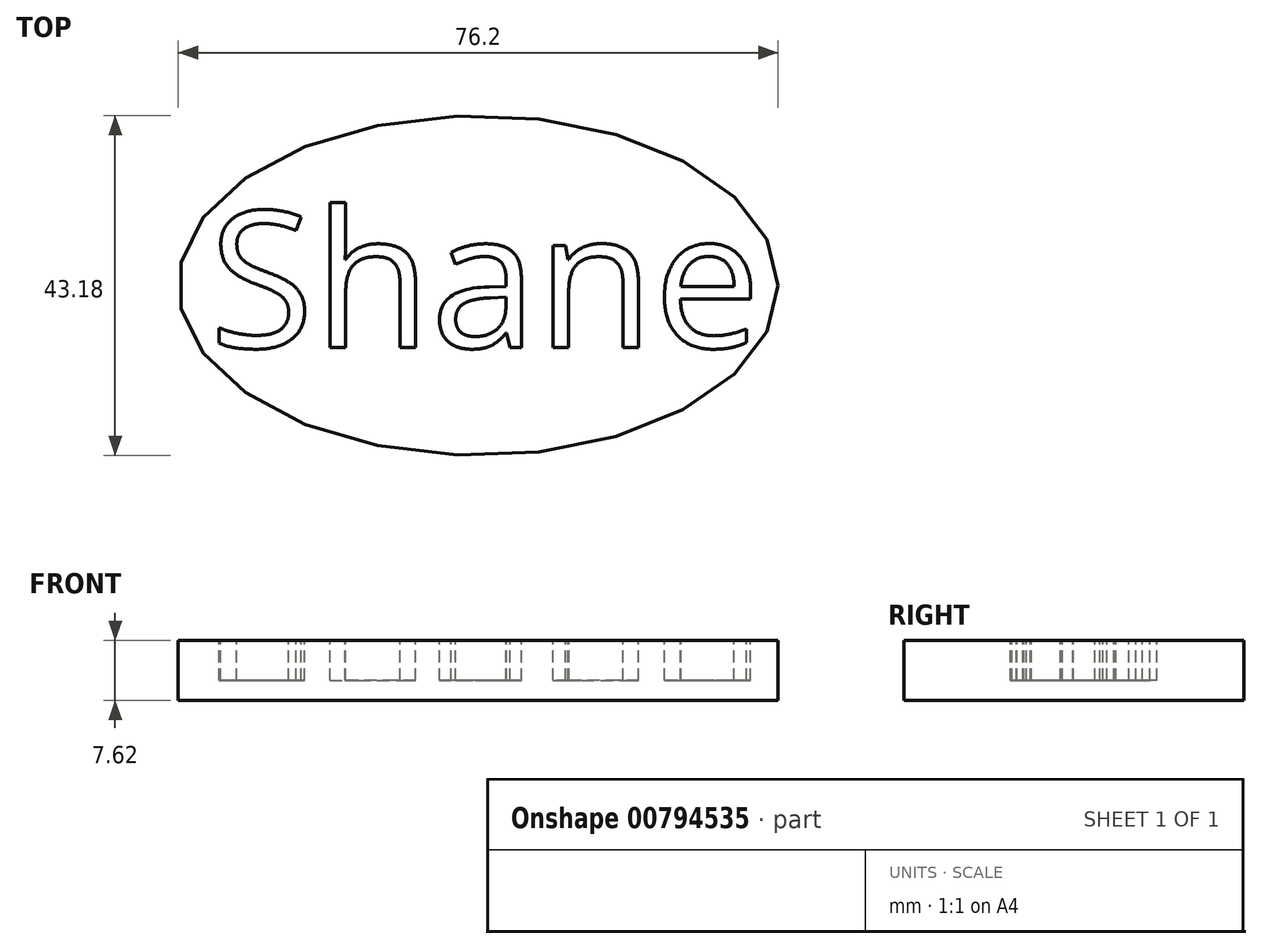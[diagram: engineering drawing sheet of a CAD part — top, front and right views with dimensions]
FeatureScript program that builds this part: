
annotation { "Feature Type Name" : "Feature", "Feature Type Description" : "" }
export const myFeature = defineFeature(function(context is Context, id is Id, definition is map)
    precondition{}
    {
        {
            var Q0;
            Q0=qCreatedBy(makeId("Top.planeOp"),FACE);
            var sketch = newSketch(context, id + "F0", { "sketchPlane" : qUnion([Q0])});
            skEllipse(sketch, "E0", {"center": v(0, 0) * mm, "majorRadius": 38.1 * mm, "minorRadius": 21.59 * mm, "majorAxis": v(1, 0)});
            skSolve(sketch);
        }
        {
            var Q0;
            Q0=makeQuery(id+"F0.imprint","IMPRINT",FACE,{"disambiguationData":[TD([[makeQuery(id+"F0.imprint","IMPRINT",EDGE,{"derivedFrom":sQuery(id+"F0.wireOp",EDGE,"E0")}),1.0]])]});
            extrude(context, id + "F1", {"entities" : qUnion([Q0]), "depth" : 7.62 * mm, "offsetDistance" : 25.4 * mm});
        }
        {
            var Q0;
            Q0=makeQuery(id+"F1.opExtrude","CAP_FACE",FACE,{"disambiguationData":[OSD([sQuery(id+"F0.wireOp",EDGE,"E0")])],"isStart":false});
            var sketch = newSketch(context, id + "F2", { "sketchPlane" : qUnion([Q0])});
            skText(sketch, "E1", { "text": "Shane\n", "fontName": "OpenSans-Regular.ttf"});
            const initialGuessF2  = {"E1": [-0.03417, -0.00787, 1, 0, 0.01743]};
            skSetInitialGuess(sketch, initialGuessF2);
            skSolve(sketch);
        }
        {
            var Q0;
            Q0 = qSketchRegion(id + "F2", true);
            extrude(context, id + "F3", {"entities" : qUnion([Q0]), "operationType" : NewBodyOperationType.REMOVE, "oppositeDirection" : true, "depth" : 5.08 * mm, "offsetDistance" : 25.4 * mm});
        }
    });
